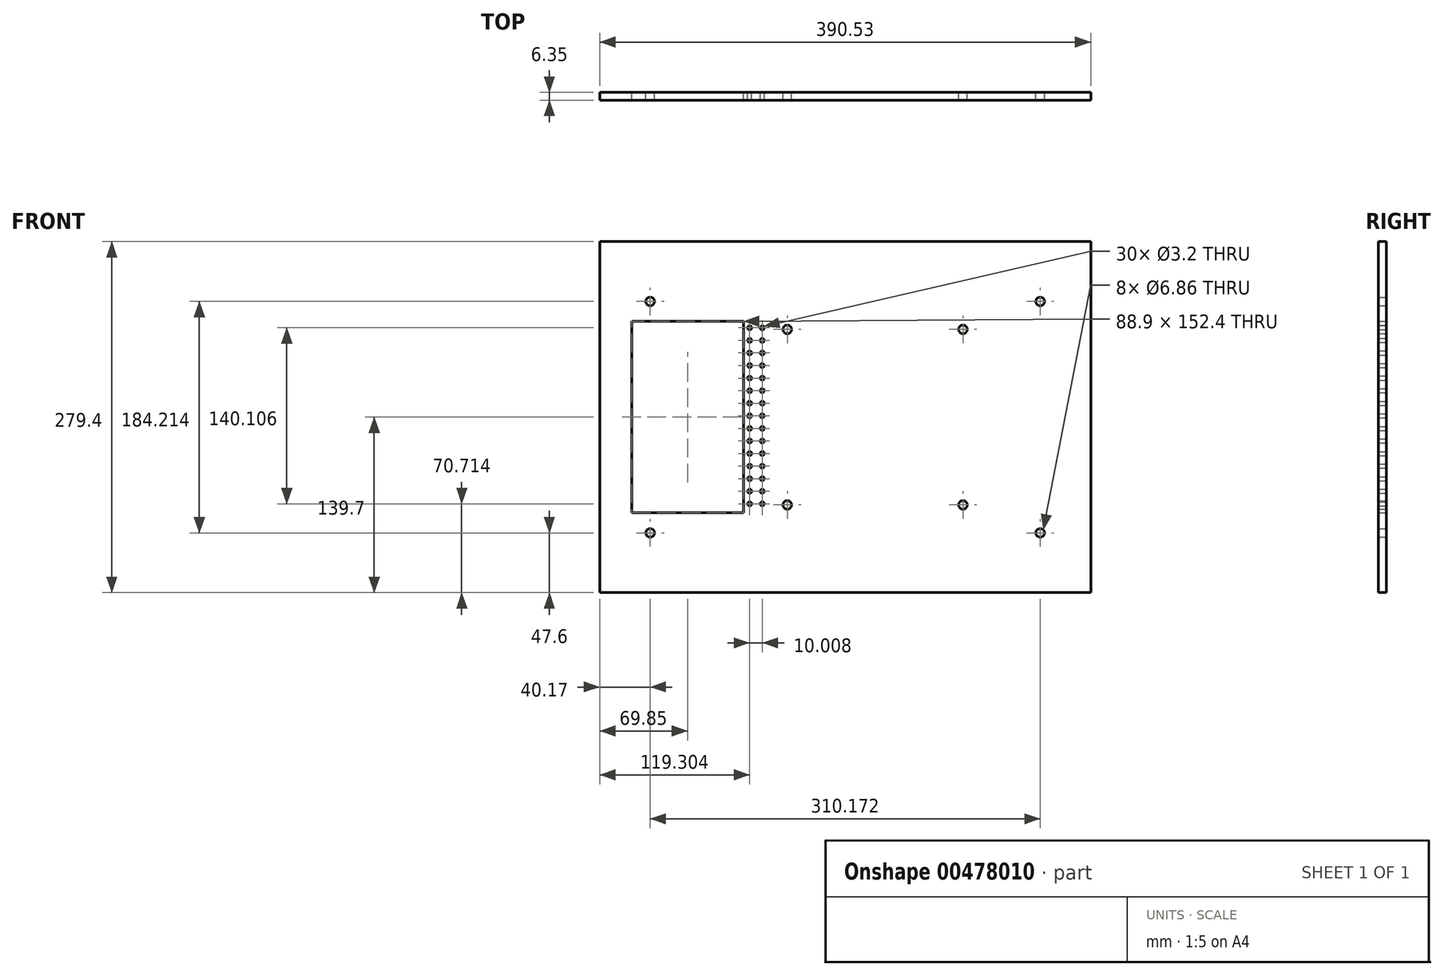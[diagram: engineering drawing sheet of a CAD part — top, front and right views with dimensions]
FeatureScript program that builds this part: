
annotation { "Feature Type Name" : "Feature", "Feature Type Description" : "" }
export const myFeature = defineFeature(function(context is Context, id is Id, definition is map)
    precondition{}
    {
        {
            var Q0;
            Q0=qCreatedBy(makeId("Front.planeOp"),FACE);
            var sketch = newSketch(context, id + "F0", { "sketchPlane" : qUnion([Q0])});
            skLineSegment(sketch, "E0.bottom", {"start": v(0, 0) * mm, "end": v(390.53, 0) * mm});
            skLineSegment(sketch, "E0.top", {"start": v(0, -279.4) * mm, "end": v(390.53, -279.4) * mm});
            skLineSegment(sketch, "E0.left", {"start": v(0, 0) * mm, "end": v(0, -279.4) * mm});
            skLineSegment(sketch, "E0.right", {"start": v(390.53, 0) * mm, "end": v(390.53, -279.4) * mm});
            skPoint(sketch, "E1.centerSnap0", {"position": v(0, -139.7) * mm});
            skPoint(sketch, "E1.centerSnap1", {"position": v(195.26, 0) * mm});
            skCircle(sketch, "E2", {"center": v(40.17, -47.59) * mm, "radius": 3.43 * mm});
            skCircle(sketch, "E3", {"center": v(40.18, -231.8) * mm, "radius": 3.43 * mm});
            skCircle(sketch, "E4", {"center": v(350.34, -47.6) * mm, "radius": 3.43 * mm});
            skCircle(sketch, "E5", {"center": v(350.34, -231.8) * mm, "radius": 3.43 * mm});
            skLineSegment(sketch, "E6.bottom", {"start": v(114.3, -63.5) * mm, "end": v(25.4, -63.5) * mm});
            skLineSegment(sketch, "E6.top", {"start": v(114.3, -215.9) * mm, "end": v(25.4, -215.9) * mm});
            skLineSegment(sketch, "E6.left", {"start": v(114.3, -63.5) * mm, "end": v(114.3, -215.9) * mm});
            skLineSegment(sketch, "E6.right", {"start": v(25.4, -63.5) * mm, "end": v(25.4, -215.9) * mm});
            skCircle(sketch, "E7", {"center": v(288.93, -69.85) * mm, "radius": 3.43 * mm});
            skCircle(sketch, "E8", {"center": v(149.22, -69.85) * mm, "radius": 3.43 * mm});
            skCircle(sketch, "E9", {"center": v(288.93, -209.55) * mm, "radius": 3.43 * mm});
            skCircle(sketch, "E10", {"center": v(149.22, -209.55) * mm, "radius": 3.43 * mm});
            skCircle(sketch, "E11", {"center": v(119.3, -68.58) * mm, "radius": 1.6 * mm});
            skCircle(sketch, "E12", {"center": v(119.3, -78.59) * mm, "radius": 1.6 * mm});
            skCircle(sketch, "E13.0.1.0", {"center": v(119.3, -88.6) * mm, "radius": 1.6 * mm});
            skCircle(sketch, "E13.0.2.0", {"center": v(119.3, -98.6) * mm, "radius": 1.6 * mm});
            skCircle(sketch, "E13.0.3.0", {"center": v(119.3, -108.61) * mm, "radius": 1.6 * mm});
            skCircle(sketch, "E13.0.4.0", {"center": v(119.3, -118.62) * mm, "radius": 1.6 * mm});
            skCircle(sketch, "E13.0.5.0", {"center": v(119.3, -128.63) * mm, "radius": 1.6 * mm});
            skCircle(sketch, "E13.0.6.0", {"center": v(119.3, -138.63) * mm, "radius": 1.6 * mm});
            skCircle(sketch, "E13.0.7.0", {"center": v(119.3, -148.64) * mm, "radius": 1.6 * mm});
            skCircle(sketch, "E13.0.8.0", {"center": v(119.3, -158.65) * mm, "radius": 1.6 * mm});
            skCircle(sketch, "E13.0.9.0", {"center": v(119.3, -168.66) * mm, "radius": 1.6 * mm});
            skCircle(sketch, "E13.0.10.0", {"center": v(119.3, -178.66) * mm, "radius": 1.6 * mm});
            skCircle(sketch, "E13.0.11.0", {"center": v(119.3, -188.67) * mm, "radius": 1.6 * mm});
            skCircle(sketch, "E13.0.12.0", {"center": v(119.3, -198.68) * mm, "radius": 1.6 * mm});
            skCircle(sketch, "E13.0.13.0", {"center": v(119.3, -208.69) * mm, "radius": 1.6 * mm});
            skLineSegment(sketch, "E13.direction1", {"start": v(119.3, -78.59) * mm, "end": v(138.35, -78.59) * mm, "construction": true});
            skLineSegment(sketch, "E13.direction2", {"start": v(119.3, -78.59) * mm, "end": v(119.3, -88.6) * mm, "construction": true});
            skCircle(sketch, "E14", {"center": v(129.31, -68.58) * mm, "radius": 1.6 * mm});
            skCircle(sketch, "E15.0.1.0", {"center": v(129.31, -78.59) * mm, "radius": 1.6 * mm});
            skLineSegment(sketch, "E15.0.1.1", {"start": v(119.3, -88.6) * mm, "end": v(119.3, -98.6) * mm, "construction": true});
            skCircle(sketch, "E15.0.2.0", {"center": v(129.31, -88.6) * mm, "radius": 1.6 * mm});
            skLineSegment(sketch, "E15.0.2.1", {"start": v(119.3, -98.6) * mm, "end": v(119.3, -108.61) * mm, "construction": true});
            skCircle(sketch, "E15.0.3.0", {"center": v(129.31, -98.6) * mm, "radius": 1.6 * mm});
            skLineSegment(sketch, "E15.0.3.1", {"start": v(119.3, -108.61) * mm, "end": v(119.3, -118.62) * mm, "construction": true});
            skCircle(sketch, "E15.0.4.0", {"center": v(129.31, -108.61) * mm, "radius": 1.6 * mm});
            skLineSegment(sketch, "E15.0.4.1", {"start": v(119.3, -118.62) * mm, "end": v(119.3, -128.63) * mm, "construction": true});
            skCircle(sketch, "E15.0.5.0", {"center": v(129.31, -118.62) * mm, "radius": 1.6 * mm});
            skLineSegment(sketch, "E15.0.5.1", {"start": v(119.3, -128.63) * mm, "end": v(119.3, -138.63) * mm, "construction": true});
            skCircle(sketch, "E15.0.6.0", {"center": v(129.31, -128.63) * mm, "radius": 1.6 * mm});
            skLineSegment(sketch, "E15.0.6.1", {"start": v(119.3, -138.63) * mm, "end": v(119.3, -148.64) * mm, "construction": true});
            skCircle(sketch, "E15.0.7.0", {"center": v(129.31, -138.63) * mm, "radius": 1.6 * mm});
            skLineSegment(sketch, "E15.0.7.1", {"start": v(119.3, -148.64) * mm, "end": v(119.3, -158.65) * mm, "construction": true});
            skCircle(sketch, "E15.0.8.0", {"center": v(129.31, -148.64) * mm, "radius": 1.6 * mm});
            skLineSegment(sketch, "E15.0.8.1", {"start": v(119.3, -158.65) * mm, "end": v(119.3, -168.66) * mm, "construction": true});
            skCircle(sketch, "E15.0.9.0", {"center": v(129.31, -158.65) * mm, "radius": 1.6 * mm});
            skLineSegment(sketch, "E15.0.9.1", {"start": v(119.3, -168.66) * mm, "end": v(119.3, -178.66) * mm, "construction": true});
            skCircle(sketch, "E15.0.10.0", {"center": v(129.31, -168.66) * mm, "radius": 1.6 * mm});
            skLineSegment(sketch, "E15.0.10.1", {"start": v(119.3, -178.66) * mm, "end": v(119.3, -188.67) * mm, "construction": true});
            skCircle(sketch, "E15.0.11.0", {"center": v(129.31, -178.66) * mm, "radius": 1.6 * mm});
            skLineSegment(sketch, "E15.0.11.1", {"start": v(119.3, -188.67) * mm, "end": v(119.3, -198.68) * mm, "construction": true});
            skCircle(sketch, "E15.0.12.0", {"center": v(129.31, -188.67) * mm, "radius": 1.6 * mm});
            skCircle(sketch, "E15.0.13.0", {"center": v(129.31, -198.68) * mm, "radius": 1.6 * mm});
            skCircle(sketch, "E15.0.14.0", {"center": v(129.31, -208.69) * mm, "radius": 1.6 * mm});
            skLineSegment(sketch, "E15.direction1", {"start": v(129.31, -68.58) * mm, "end": v(148.36, -68.58) * mm, "construction": true});
            skLineSegment(sketch, "E15.direction2", {"start": v(129.31, -68.58) * mm, "end": v(129.31, -78.59) * mm, "construction": true});
            skSolve(sketch);
        }
        {
            var Q0;
            Q0=makeQuery(id+"F0.imprint","IMPRINT",FACE,{"disambiguationData":[TD([[makeQuery(id+"F0.imprint","IMPRINT",EDGE,{"derivedFrom":sQuery(id+"F0.wireOp",EDGE,"E0.bottom")}),-1.0]])]});
            var Q1;
            Q1=makeQuery(id+"F0.imprint","IMPRINT",FACE,{"disambiguationData":[TD([[makeQuery(id+"F0.imprint","IMPRINT",EDGE,{"derivedFrom":sQuery(id+"F0.wireOp",EDGE,"lb0dudhl-Vc2p-vhzT-qKrT-u36RMP7FULvm")}),-1.0]])]});
            var Q2;
            Q2=makeQuery(id+"F0.imprint","IMPRINT",FACE,{"disambiguationData":[TD([[makeQuery(id+"F0.imprint","IMPRINT",EDGE,{"derivedFrom":sQuery(id+"F0.wireOp",EDGE,"3c71f504-c0a2-4175-b601-4670770f8600")}),-1.0]])]});
            var Q3;
            {var subQ4=sQuery(id+"F0.wireOp",EDGE,"b47da31c-8649-4bed-b1c1-519669b31e82");Q3=makeQuery(id+"F0.imprint","IMPRINT",FACE,{"disambiguationData":[TD([[makeQuery(id+"F0.imprint","IMPRINT",EDGE,{"derivedFrom":subQ4}),-1.0]])]});}
            var Q4;
            {var subQ0=sQuery(id+"F0.wireOp",EDGE,"d6b5375b-6ece-49c0-9899-6c22bac9c5f5");Q4=makeQuery(id+"F0.imprint","IMPRINT",FACE,{"disambiguationData":[TD([[makeQuery(id+"F0.imprint","IMPRINT",EDGE,{"derivedFrom":subQ0}),-1.0]])]});}
            var Q5;
            Q5=makeQuery(id+"F0.imprint","IMPRINT",FACE,{"disambiguationData":[TD([[makeQuery(id+"F0.imprint","IMPRINT",EDGE,{"derivedFrom":sQuery(id+"F0.wireOp",EDGE,"z1qTjQIb-Jimh-9hqU-JySS-5MLiwB3lGvNS")}),1.0]])]});
            var Q6;
            {var subQ0=sQuery(id+"F0.wireOp",EDGE,"tfCknZIC-cQV1-Gq0s-NfXF-kksXRXzh9ulT");var subQ1=sQuery(id+"F0.wireOp",EDGE,"u6DDQtYM-Ebng-WeWw-w95z-C9bbfhq54Dpc");var subQ2=makeQuery(id+"F0.imprint","INTERSECT",VERTEX,{"disambiguationData":[OD(0.0)],"derivedFrom":[subQ1,subQ0]});Q6=makeQuery(id+"F0.imprint","IMPRINT",FACE,{"disambiguationData":[TD([[makeQuery(id+"F0.imprint","IMPRINT",EDGE,{"disambiguationData":[TD([[subQ2,-1.0]])],"derivedFrom":subQ1}),-1.0]])]});}
            extrude(context, id + "F1", {"entities" : qUnion([Q0, Q1, Q2, Q3, Q4, Q5, Q6]), "depth" : 6.35 * mm});
        }
    });
